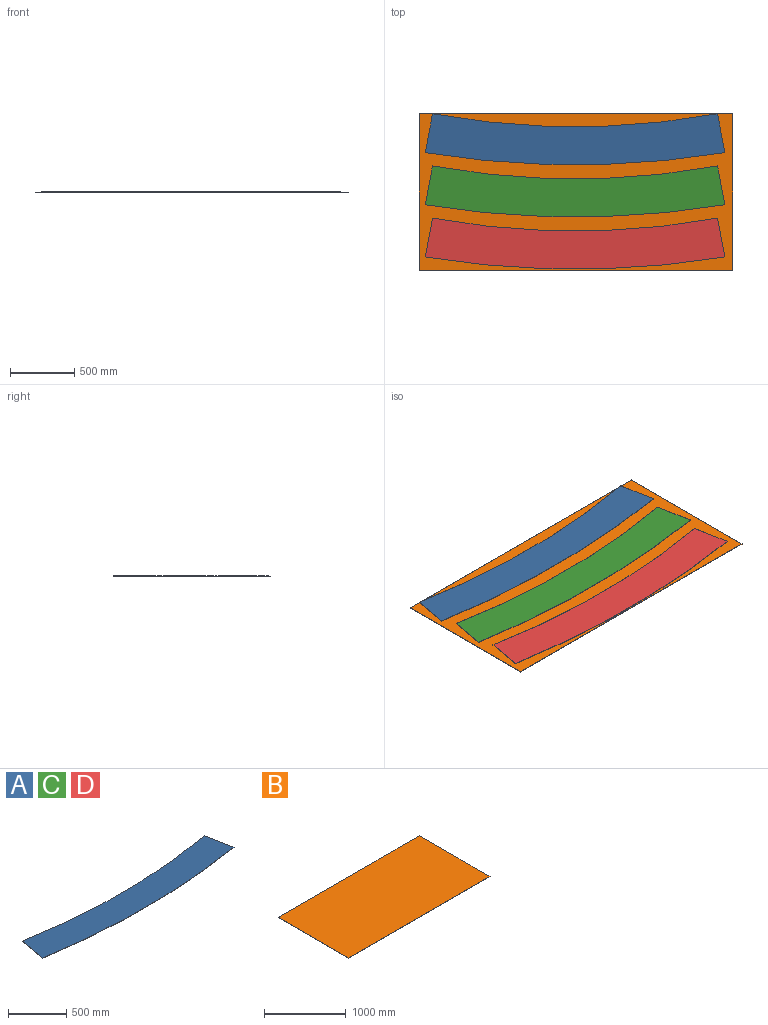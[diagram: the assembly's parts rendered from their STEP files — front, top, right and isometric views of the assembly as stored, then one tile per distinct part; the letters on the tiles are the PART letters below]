
ASSEMBLY  parts=4 mates=1
PART A: 6 faces, bbox 2332.7x397.9x3.2 mm
  f0: plane 2332.65x397.89mm, normal (0,0,1), area 686323.1mm2, adj f2,f3,f4,f5
  f1: plane 2332.65x397.89mm, normal (0,0,-1), area 686323.1mm2, adj f2,f3,f4,f5
  f2: cylinder r=6096mm len=2220.44mm, axis (0,0,1), area 7089.5mm2, adj f0,f1,f3,f4
  f3: plane 302.93x56.11mm, normal (-0.98,0.18,0), area 978.1mm2, adj f0,f1,f2,f5
  f4: plane 302.93x56.11mm, normal (0.98,0.18,0), area 978.1mm2, adj f0,f1,f2,f5
  f5: cylinder r=7210.07mm len=2332.65mm, axis (0,0,1), area 7438.9mm2, adj f0,f1,f3,f4
PART B: 6 faces, bbox 2438.4x1219.2x3.2 mm
  f0: plane 2438.4x3.18mm, normal (0,1,0), area 7741.9mm2, adj f1,f3,f4,f5
  f1: plane 1219.2x3.18mm, normal (-1,0,0), area 3871mm2, adj f0,f2,f4,f5
  f2: plane 2438.4x3.18mm, normal (0,-1,0), area 7741.9mm2, adj f1,f3,f4,f5
  f3: plane 1219.2x3.18mm, normal (1,0,0), area 3871mm2, adj f0,f2,f4,f5
  f4: plane 2438.4x1219.2mm, normal (0,0,1), area 2972897.3mm2, adj f0,f1,f2,f3
  f5: plane 2438.4x1219.2mm, normal (0,0,-1), area 2972897.3mm2, adj f0,f1,f2,f3
PART C: same geometry as A
PART D: same geometry as A
PLACE A t=(-7.38,21.21,3.18)mm
PLACE B at identity
PLACE C t=(-7.38,-385.19,3.18)mm
PLACE D t=(-7.38,-791.59,3.18)mm
MATE fastened B.f4 <-> A.f1  axis (0,0,1) through (-1219.2,609.6,3.18)mm
